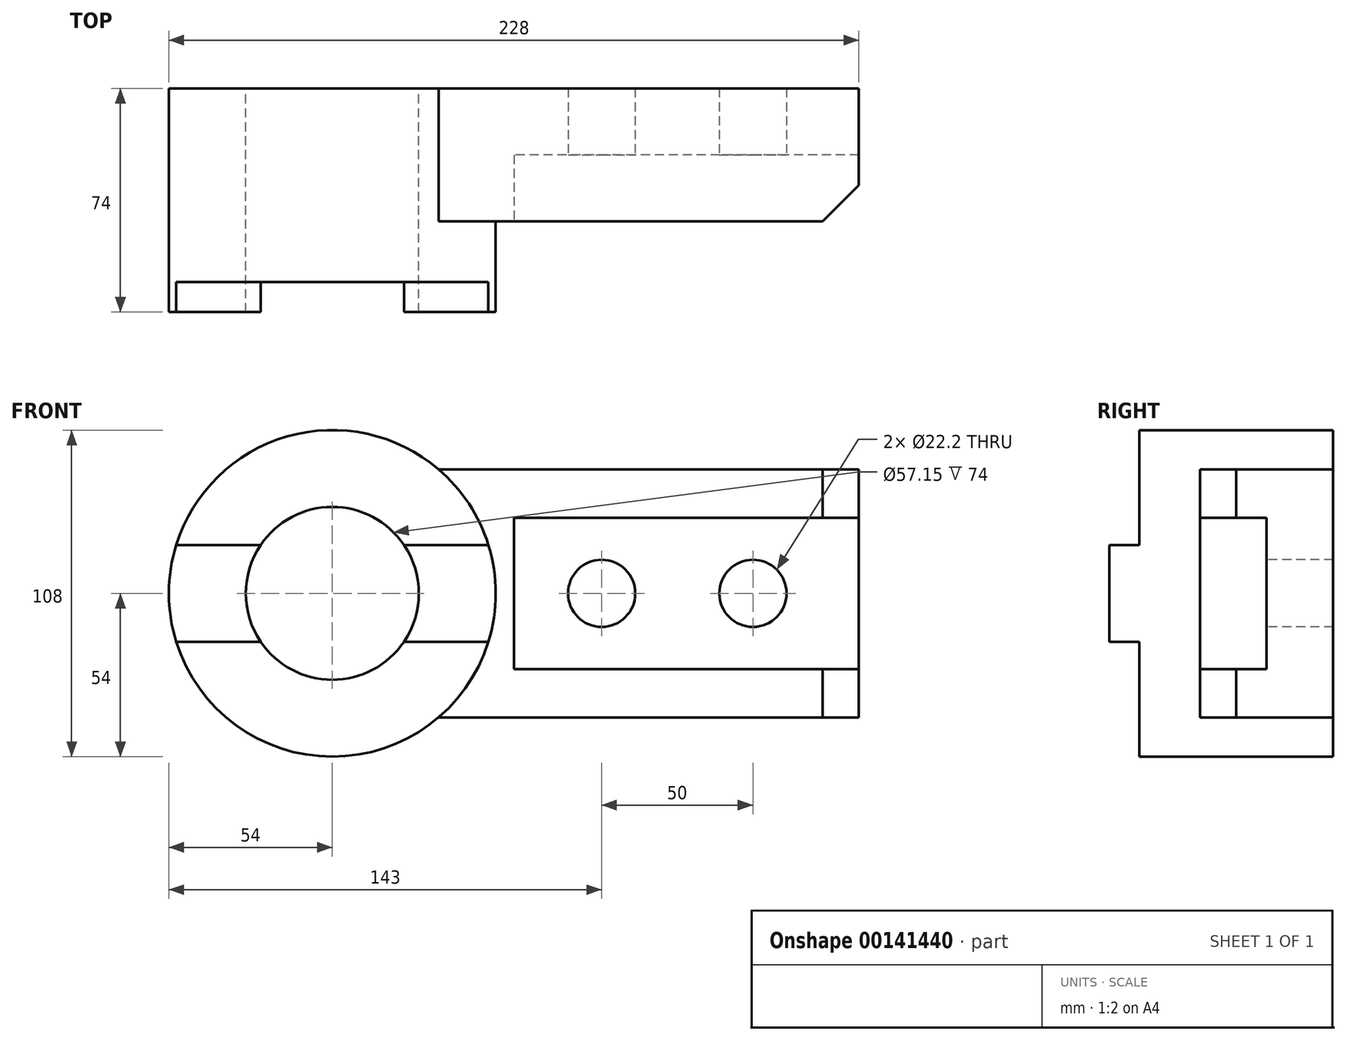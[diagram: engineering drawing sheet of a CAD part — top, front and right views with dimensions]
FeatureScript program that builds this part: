
annotation { "Feature Type Name" : "Feature", "Feature Type Description" : "" }
export const myFeature = defineFeature(function(context is Context, id is Id, definition is map)
    precondition{}
    {
        {
            var Q0;
            Q0=qCreatedBy(makeId("Front.planeOp"),FACE);
            var sketch = newSketch(context, id + "F0", { "sketchPlane" : qUnion([Q0])});
            skCircle(sketch, "E0", {"center": v(0, 0) * mm, "radius": 28.57 * mm});
            skCircle(sketch, "E1", {"center": v(0, 0) * mm, "radius": 54 * mm});
            skSolve(sketch);
        }
        {
            var Q0;
            Q0 = qSketchRegion(id + "F0", true);
            extrude(context, id + "F1", {"entities" : qUnion([Q0]), "endBound" : BoundingType.SYMMETRIC, "depth" : 64 * mm});
        }
        {
            var Q0;
            Q0=makeQuery(id+"F1.opExtrude","CAP_FACE",FACE,{"disambiguationData":[OSD([sQuery(id+"F0.wireOp",EDGE,"E0"),sQuery(id+"F0.wireOp",EDGE,"E1")])],"isStart":false});
            var sketch = newSketch(context, id + "F2", { "sketchPlane" : qUnion([Q0])});
            skLineSegment(sketch, "E2", {"start": v(-51.58, -16) * mm, "end": v(-23.68, -16) * mm});
            skArc(sketch, "E3", {"start": v(-23.68, 16) * mm, "mid": v(-28.58, 0) * mm, "end": v(-23.68, -16) * mm});
            skLineSegment(sketch, "E4", {"start": v(-23.68, 16) * mm, "end": v(-51.58, 16) * mm});
            skArc(sketch, "E5", {"start": v(-51.58, 16) * mm, "mid": v(-54, 0) * mm, "end": v(-51.58, -16) * mm});
            skLineSegment(sketch, "E6", {"start": v(23.68, -16) * mm, "end": v(51.58, -16) * mm});
            skArc(sketch, "E7", {"start": v(51.58, -16) * mm, "mid": v(54, 0) * mm, "end": v(51.58, 16) * mm});
            skLineSegment(sketch, "E8", {"start": v(51.58, 16) * mm, "end": v(23.68, 16) * mm});
            skArc(sketch, "E9", {"start": v(23.68, -16) * mm, "mid": v(28.57, 0) * mm, "end": v(23.68, 16) * mm});
            skSolve(sketch);
        }
        {
            var Q0;
            Q0 = qSketchRegion(id + "F2", true);
            extrude(context, id + "F3", {"entities" : qUnion([Q0]), "operationType" : NewBodyOperationType.ADD, "depth" : 10 * mm});
        }
        {
            var Q0;
            Q0=qCreatedBy(makeId("Front.planeOp"),FACE);
            var sketch = newSketch(context, id + "F4", { "sketchPlane" : qUnion([Q0])});
            skLineSegment(sketch, "E10", {"start": v(35.14, 41) * mm, "end": v(174, 41) * mm});
            skLineSegment(sketch, "E11", {"start": v(174, 41) * mm, "end": v(174, -41) * mm});
            skLineSegment(sketch, "E12.bottom", {"start": v(174, 25) * mm, "end": v(60, 25) * mm});
            skLineSegment(sketch, "E12.top", {"start": v(174, -25) * mm, "end": v(60, -25) * mm});
            skLineSegment(sketch, "E12.left", {"start": v(174, 25) * mm, "end": v(174, -25) * mm});
            skLineSegment(sketch, "E12.right", {"start": v(60, 25) * mm, "end": v(60, -25) * mm});
            skLineSegment(sketch, "E13", {"start": v(174, -41) * mm, "end": v(35.14, -41) * mm});
            skCircle(sketch, "E14", {"center": v(89, 0) * mm, "radius": 11.1 * mm});
            skCircle(sketch, "E15", {"center": v(139, 0) * mm, "radius": 11.1 * mm});
            skArc(sketch, "E16", {"start": v(35.14, -41) * mm, "mid": v(54, 0) * mm, "end": v(35.14, 41) * mm});
            skSolve(sketch);
        }
        {
            var Q0;
            {var subQ2=sQuery(id+"F4.wireOp",EDGE,"E10");Q0=makeQuery(id+"F4.imprint","IMPRINT",FACE,{"disambiguationData":[TD([[makeQuery(id+"F4.imprint","IMPRINT",EDGE,{"derivedFrom":subQ2}),-1.0]])]});}
            extrude(context, id + "F5", {"entities" : qUnion([Q0]), "operationType" : NewBodyOperationType.ADD, "oppositeDirection" : true, "depth" : 32 * mm, "hasSecondDirection" : true, "secondDirectionOppositeDirection" : false, "secondDirectionDepth" : 12 * mm});
        }
        {
            var Q0;
            Q0=makeQuery(id+"F4.imprint","IMPRINT",FACE,{"disambiguationData":[TD([[makeQuery(id+"F4.imprint","IMPRINT",EDGE,{"derivedFrom":sQuery(id+"F4.wireOp",EDGE,"E12.bottom")}),1.0]])]});
            extrude(context, id + "F6", {"entities" : qUnion([Q0]), "operationType" : NewBodyOperationType.ADD, "oppositeDirection" : true, "depth" : 32 * mm});
        }
        {
            var Q0;
            Q0=makeQuery(id+"F4.imprint","IMPRINT",FACE,{"disambiguationData":[TD([[makeQuery(id+"F4.imprint","IMPRINT",EDGE,{"derivedFrom":sQuery(id+"F4.wireOp",EDGE,"E12.bottom")}),1.0]])]});
            extrude(context, id + "F7", {"entities" : qUnion([Q0]), "operationType" : NewBodyOperationType.REMOVE, "oppositeDirection" : true, "depth" : 10 * mm});
        }
        {
            var Q0;
            Q0=makeQuery(id+"F5.opExtrude","SWEPT_FACE",FACE,{"disambiguationData":[OSD([sQuery(id+"F4.wireOp",EDGE,"E13")])]});
            var sketch = newSketch(context, id + "F8", { "sketchPlane" : qUnion([Q0])});
            skLineSegment(sketch, "E17", {"start": v(162, 12) * mm, "end": v(174, 0) * mm});
            skLineSegment(sketch, "E18", {"start": v(174, 0) * mm, "end": v(174, 12) * mm});
            skLineSegment(sketch, "E19", {"start": v(174, 12) * mm, "end": v(162, 12) * mm});
            skSolve(sketch);
        }
        {
            var Q0;
            Q0 = qSketchRegion(id + "F8", true);
            extrude(context, id + "F9", {"entities" : qUnion([Q0]), "operationType" : NewBodyOperationType.REMOVE, "endBound" : BoundingType.THROUGH_ALL, "oppositeDirection" : true, "depth" : 25 * mm});
        }
    });
